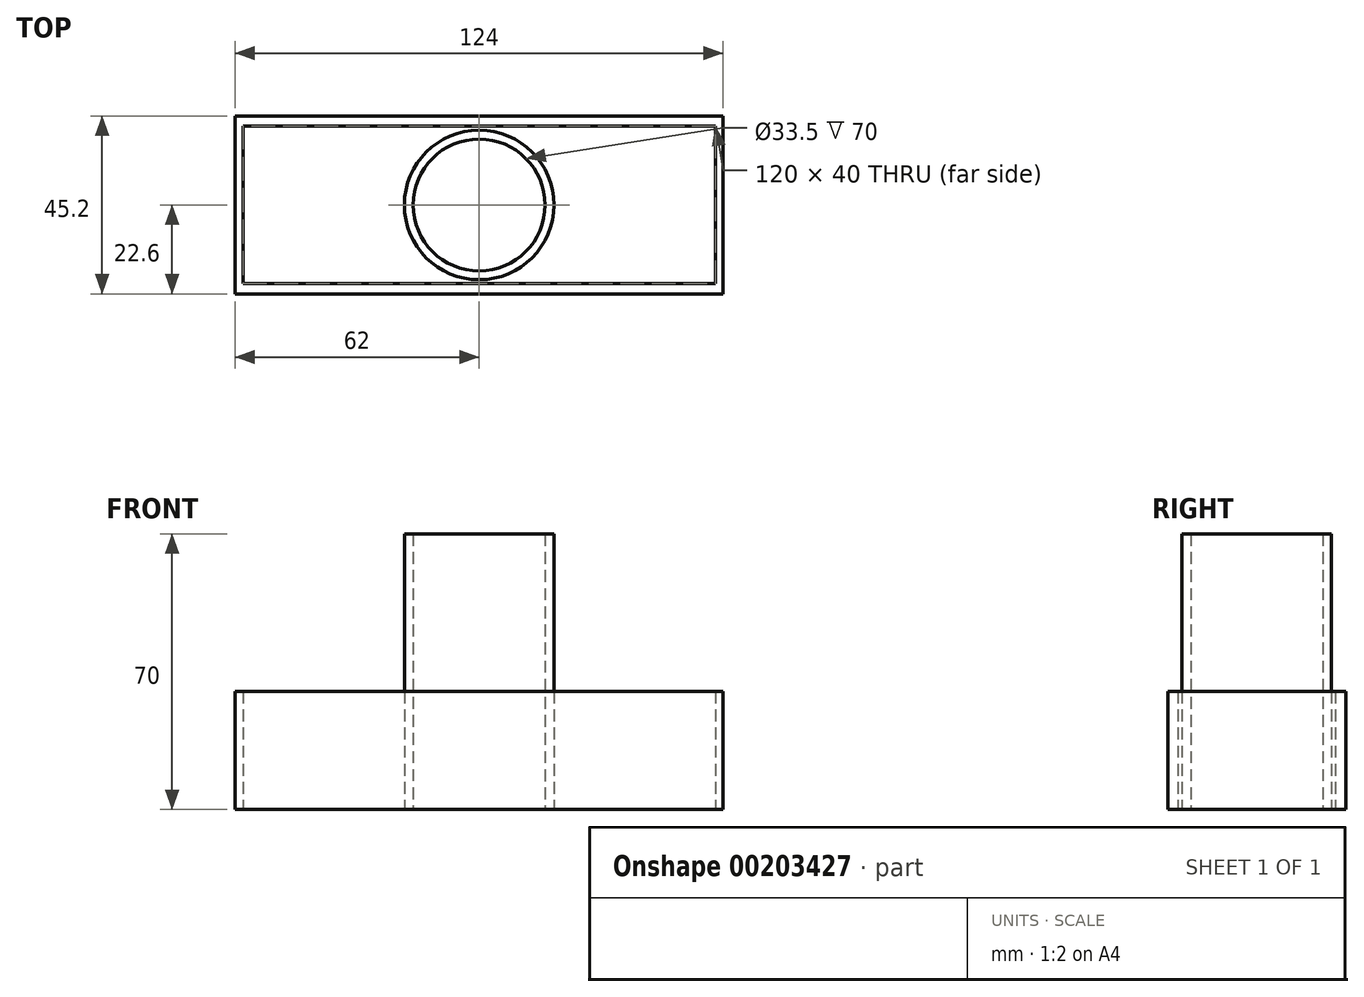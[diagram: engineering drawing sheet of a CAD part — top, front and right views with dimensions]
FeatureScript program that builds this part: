
annotation { "Feature Type Name" : "Feature", "Feature Type Description" : "" }
export const myFeature = defineFeature(function(context is Context, id is Id, definition is map)
    precondition{}
    {
        {
            var Q0;
            Q0=qCreatedBy(makeId("Top.planeOp"),FACE);
            var sketch = newSketch(context, id + "F0", { "sketchPlane" : qUnion([Q0])});
            skCircle(sketch, "E0", {"center": v(0, 0) * mm, "radius": 16.75 * mm});
            skLineSegment(sketch, "E1", {"start": v(0, 0) * mm, "end": v(0, 16.75) * mm});
            skLineSegment(sketch, "E2", {"start": v(0, 16.75) * mm, "end": v(0, 19) * mm});
            skCircle(sketch, "E3", {"center": v(0, 0) * mm, "radius": 19 * mm});
            skSolve(sketch);
        }
        {
            var Q0;
            Q0=makeQuery(id+"F0.imprint","IMPRINT",FACE,{"disambiguationData":[TD([[makeQuery(id+"F0.imprint","IMPRINT",EDGE,{"derivedFrom":sQuery(id+"F0.wireOp",EDGE,"E0")}),-1.0]])]});
            extrude(context, id + "F1", {"entities" : qUnion([Q0]), "depth" : 70 * mm});
        }
        {
            var Q0;
            Q0=qCreatedBy(makeId("Top.planeOp"),FACE);
            var sketch = newSketch(context, id + "F2", { "sketchPlane" : qUnion([Q0])});
            skLineSegment(sketch, "E4.bottom", {"start": v(60, 20) * mm, "end": v(-60, 20) * mm});
            skLineSegment(sketch, "E4.top", {"start": v(60, -20) * mm, "end": v(-60, -20) * mm});
            skLineSegment(sketch, "E4.left", {"start": v(60, 20) * mm, "end": v(60, -20) * mm});
            skLineSegment(sketch, "E4.right", {"start": v(-60, 20) * mm, "end": v(-60, -20) * mm});
            skPoint(sketch, "E4.middle", {"position": v(0, 0) * mm});
            skLineSegment(sketch, "E5.bottom", {"start": v(62, -22.6) * mm, "end": v(-62, -22.6) * mm});
            skLineSegment(sketch, "E5.top", {"start": v(62, 22.6) * mm, "end": v(-62, 22.6) * mm});
            skLineSegment(sketch, "E5.left", {"start": v(62, -22.6) * mm, "end": v(62, 22.6) * mm});
            skLineSegment(sketch, "E5.right", {"start": v(-62, -22.6) * mm, "end": v(-62, 22.6) * mm});
            skSolve(sketch);
        }
        {
            var Q0;
            Q0=makeQuery(id+"F2.imprint","IMPRINT",FACE,{"disambiguationData":[TD([[makeQuery(id+"F2.imprint","IMPRINT",EDGE,{"derivedFrom":sQuery(id+"F2.wireOp",EDGE,"E4.bottom")}),-1.0]])]});
            extrude(context, id + "F3", {"entities" : qUnion([Q0]), "depth" : 30 * mm});
        }
    });
